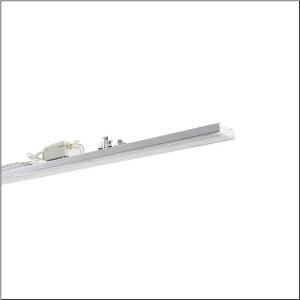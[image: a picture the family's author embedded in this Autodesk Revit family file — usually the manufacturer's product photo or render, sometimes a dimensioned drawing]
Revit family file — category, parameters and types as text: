
# Revit family: licross_21_recessed_mo_52tl18mn4a5g
name_source: partatom
category: Lighting Fixtures
units: mm (PartAtom-declared; Revit-internal decimal feet)

## family parameters
Cut with Voids When Loaded = No
Host = Face
Light Source = No
Part Type = Normal
Room Calculation Point = No
Round Connector Dimension = Use Diameter
Shared = No

## types (1)
- --- (1 x LED, 10680 lm, 60.5 W, 4000K)
    Apparent Load = 61 VA
    CIE Flux Codes = 79 95 99 100 100
    Color Rendering = 80
    Color Temperature = 4000K
    Default Elevation = 1800 mm
    Description = Licross 21 Recessed MO, luminaire insert, of sheet steel, galvanised, coil coated, white, length: 1.500mm, width: 66mm, height: 67mm, LED rated luminous flux: 10.680lm, light colour: 840, SDCM (Standard Deviation of Colour Matching)MacAdam ≤ 3 SDCM (initial), control gear: ON/OFF Multilumen, with plug, 3-pole, with phase selection, mains connection: 220..240V, AC, 50/60Hz, rated input power: 61W, internal wiring halogen-free, primary light control with lens, of plastic, primary optical cover: cover, of PMMA, light emission: direct distribution, primary light characteristic: symmetric, protection rating (complete): IP40, insulation class (complete): insulation class I (protective earthing), certification: CE, ENEC, VDE, UKCA, protection symbol: D if used in an environment without relevant dust loads with corresponding accessories, impact resistance: IK06, permissible ambient temperature for indoor applications: -35..+40°C, corresponds to IFS (International Featured Standards) requirements for safety and quality in the food industry, reducing of maximum allowable ambient temperature of 5°C with ceiling mounting, LABS conformity tested according to VDMA 24364:2018-05, The light source and the operating device comply with the requirements of the Ecodesign Regulation (EU) 2019/2020 and are replaceable in accordance with this regulation, packaging unit: 1 piece
    Height = 58 mm
    Lamp = 1 x LED
    Lamp Light Flux = 10680 lm
    Lamp Power = 60.5 W
    Lamp count = 1
    Length = 1500 mm
    Luminous efficacy = 177 lm/W
    Manufacturer = Siteco
    ModVariant = No
    Model = 52TL18MN4A5G
    Mounting Place = Ceiling
    Mounting Type = Pendant
    Number of Poles = 1
    OnlyDefault = Yes
    Power Factor = 1
    Product Name = Licross 21 Recessed MO
    Product group = luminaire insert | ceiling pendant
    ProductGroupID = 901
    Protection Class = Protection class I
    Protection Degree = IP 40
    RLX_Detail_Level = 1
    RLX_Emergency_Light_Flux = 0 lm
    RLX_Emergency_Type = 0
    RLX_Emergency_Type_DB = No
    RlxData = <blob elided: 22537 chars, md5=53aab715>
    Socket = socket
    Standby Power = 0 W
    System Light Flux = 10680 lm
    System Power = 61 W
    Type Comments = factory setting: luminous flux: 100 % | (A | C | E) | 140 mA
    Type Image = l_1296930.jpg
    URL = http://relux.com
    VarID = @adj_109503
    Voltage = 0 V
    Weight = 0.00 kg
    Width = 66 mm

## geometry (parser evidence)
native form markers: Blend x4, Sweep x12
no freeform markers — native parametric forms only
